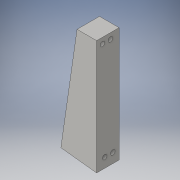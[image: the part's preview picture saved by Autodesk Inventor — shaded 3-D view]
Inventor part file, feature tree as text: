
AUTODESK INVENTOR PART (.ipt)
format: ipt  version: 2016 (Build 200138000, 138)  size: 111,616 bytes
history: native  units: in
note: dims shown in document units (in); Inventor stores cm internally (conversion verified against a paired STEP export)
features: extrude x2, sketch x2
ambient origin geometry x8: Origin, YZ Plane, XZ Plane, XY Plane, X Axis, Y Axis, Z Axis, Center Point
bodies: Solid1 (feature_tree)
feature tree (4):
  extrude  "Extrusion1"  Depth=2.4409in
  extrude  "Extrusion2"  Depth=0.3937in
  sketch  "Sketch1"  dims[d0=7.8346in d1=2.4409in]
  sketch  "Sketch2"  dims[d2=1.3386in d3=0.2756in d4=1.5354in d5=0.0in d6=0.315in d7=0.315in d8=0.5512in d9=0.5512in d10=6.7717in d11=0.315in d12=0.315in d13=0.5512in d14=0.3937in d16=1.5354in d17=0.0in d18=0.3937in]
